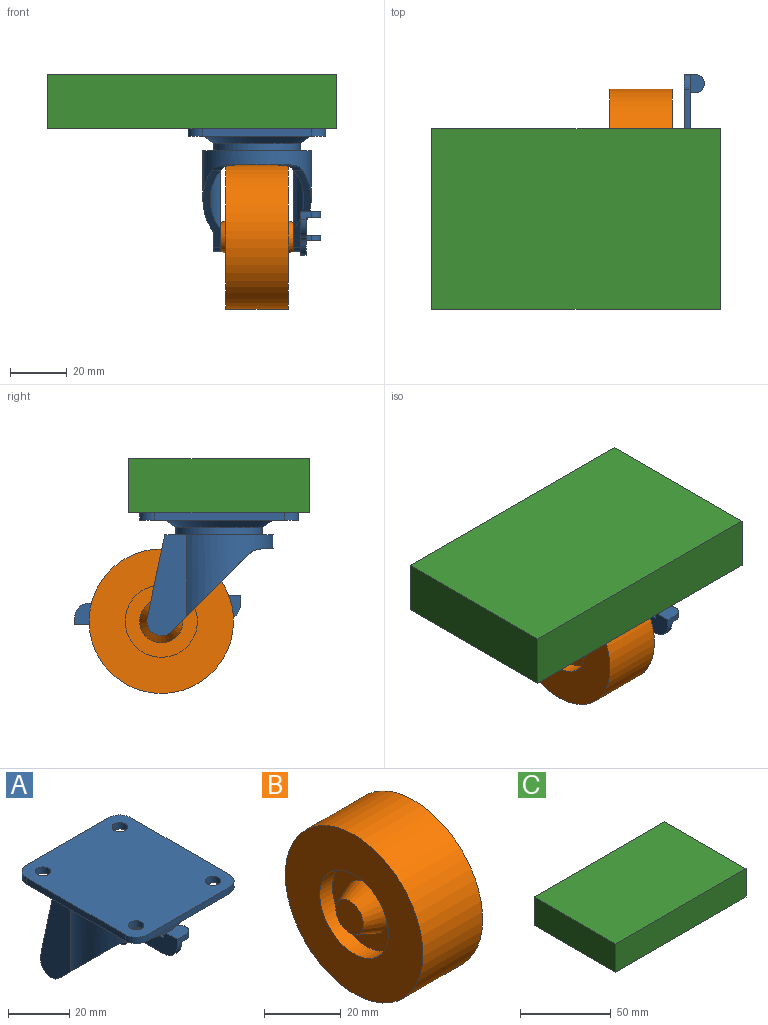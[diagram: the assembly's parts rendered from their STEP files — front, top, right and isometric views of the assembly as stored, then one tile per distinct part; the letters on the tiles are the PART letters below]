
ASSEMBLY  parts=3 mates=2
PART A: 53 faces, bbox 48.3x78.7x44.5 mm
  f0: plane 24.13x12.74mm, normal (1,0,0), area 245.6mm2, adj f5,f6,f11,f16
  f1: cylinder r=5.08mm len=8.67mm, axis (1,0,0), area 33.1mm2, adj f3,f11,f14,f17
  f2: cylinder r=6.35mm len=8.84mm, axis (1,0,0), area 18.4mm2, adj f5,f8,f9,f13
  f3: plane 27.13x27.13mm, normal (0,-0.71,-0.71), area 94.3mm2, adj f1,f5,f7,f13,f14,f17,f19,f32
  f4: plane 35.56x13.97mm, normal (-1,0,0), area 372.6mm2, adj f5,f6,f9,f10,f11
  f5: cylinder r=19.05mm len=38.1mm, axis (0,0,-1), area 1021.3mm2, adj f0,f2,f3,f4,f6,f7,f8,f9
  f6: plane 38.1x38.1mm, normal (0,0,1), area 480.4mm2, adj f0,f4,f5,f11,f37
  f7: cylinder r=6.35mm len=8.84mm, axis (1,0,0), area 18.4mm2, adj f3,f5,f8,f13
  f8: plane 23.75x4.16mm, normal (0,0,-1), area 51.9mm2, adj f2,f5,f7,f13
  f9: plane 27.13x27.13mm, normal (0,-0.71,-0.71), area 103.1mm2, adj f2,f4,f5,f10,f12,f13
  f10: cylinder r=5.08mm len=8.67mm, axis (1,0,0), area 33.1mm2, adj f4,f9,f11,f12
  f11: plane 30.48x29.43mm, normal (0,0.98,0.21), area 218.8mm2, adj f0,f1,f4,f6,f10,f12,f14,f15
  f12: plane 33.02x14.85mm, normal (1,0,0), area 375.2mm2, adj f9,f10,f11,f13,f15
  f13: cylinder r=16.51mm len=33.02mm, axis (0,0,-1), area 757.9mm2, adj f2,f3,f7,f8,f9,f12,f14,f15
  f14: plane 33.02x14.85mm, normal (-1,0,0), area 375.2mm2, adj f1,f3,f11,f13,f15
  f15: plane 36.1x33.02mm, normal (0,0,-1), area 980.7mm2, adj f11,f12,f13,f14
  f16: plane 37.68x2.03mm, normal (0,0,1), area 72.9mm2, adj f0,f5,f17,f18,f32
  f17: plane 58.42x15.24mm, normal (-1,0,0), area 308.3mm2, adj f1,f3,f11,f16,f18,f19,f20,f21
  f18: cylinder r=5.08mm len=5.08mm, axis (-1,0,0), area 16.2mm2, adj f16,f17,f31,f32
  f19: plane 8.06x2.03mm, normal (0,0,1), area 16.4mm2, adj f3,f17,f20,f32
  f20: plane 3.94x2.54mm, normal (0,1,0), area 9mm2, adj f17,f19,f21,f32,f33,f36
  f21: plane 7.11x6.35mm, normal (0,0,1), area 40.8mm2, adj f17,f20,f22,f36
  f22: plane 3.94x2.54mm, normal (0,-1,0), area 9mm2, adj f17,f21,f23,f32,f33,f36
  f23: cylinder r=6.35mm len=6.35mm, axis (-1,0,0), area 20.3mm2, adj f17,f22,f24,f32
  f24: plane 13.07x2.03mm, normal (0,0,-1), area 26.6mm2, adj f17,f23,f25,f32
  f25: cylinder r=2.54mm len=2.43mm, axis (-1,0,0), area 6.6mm2, adj f17,f24,f26,f32
  f26: cylinder r=6.35mm len=12.17mm, axis (-1,0,0), area 33.1mm2, adj f17,f25,f27,f32
  f27: cylinder r=2.54mm len=2.43mm, axis (-1,0,0), area 6.6mm2, adj f17,f26,f28,f32
  f28: plane 15.61x2.03mm, normal (0,0,-1), area 31.7mm2, adj f17,f27,f29,f32
  f29: plane 3.94x2.03mm, normal (0,-1,0), area 6.5mm2, adj f17,f28,f30,f32,f34,f35
  f30: plane 7.11x6.35mm, normal (0,0,-1), area 40.8mm2, adj f17,f29,f31,f35
  f31: plane 3.94x2.54mm, normal (0,1,0), area 9mm2, adj f17,f18,f30,f32,f34,f35
  f32: plane 58.42x13.21mm, normal (1,0,0), area 419.4mm2, adj f3,f5,f16,f18,f19,f20,f22,f23
  f33: plane 6.35x5.08mm, normal (0,0,-1), area 27.9mm2, adj f20,f22,f32,f36
  f34: plane 6.35x5.08mm, normal (0,0,1), area 27.9mm2, adj f29,f31,f32,f35
  f35: cylinder r=3.17mm len=6.35mm, axis (0,0,-1), area 20.3mm2, adj f29,f30,f31,f34
  f36: cylinder r=3.17mm len=6.35mm, axis (0,0,1), area 20.3mm2, adj f20,f21,f22,f33
  f37: cylinder r=15.24mm len=30.48mm, axis (0,0,-1), area 243.2mm2, adj f6,f38
  f38: cone r=15.24mm half-angle=56.3deg, axis (0,0,1), area 493.3mm2, adj f37,f48
  f39: plane 38.1x2.54mm, normal (0,1,0), area 96.8mm2, adj f47,f48,f49,f52
  f40: plane 45.72x2.54mm, normal (-1,0,0), area 116.1mm2, adj f47,f48,f49,f50
  f41: plane 38.1x2.54mm, normal (0,-1,0), area 96.8mm2, adj f47,f48,f50,f51
  f42: cylinder r=2.54mm len=5.08mm, axis (0,0,-1), area 40.5mm2, adj f47,f48
  f43: cylinder r=2.54mm len=5.08mm, axis (0,0,-1), area 40.5mm2, adj f47,f48
  f44: cylinder r=2.54mm len=5.08mm, axis (0,0,-1), area 40.5mm2, adj f47,f48
  f45: cylinder r=2.54mm len=5.08mm, axis (0,0,-1), area 40.5mm2, adj f47,f48
  f46: plane 45.72x2.54mm, normal (1,0,0), area 116.1mm2, adj f47,f48,f51,f52
  f47: plane 55.88x48.26mm, normal (0,0,1), area 2593.5mm2, adj f39,f40,f41,f42,f43,f44,f45,f46
  f48: plane 55.88x48.26mm, normal (0,0,-1), area 1453.5mm2, adj f38,f39,f40,f41,f42,f43,f44,f45
  f49: cylinder r=5.08mm len=5.08mm, axis (0,0,1), area 20.3mm2, adj f39,f40,f47,f48
  f50: cylinder r=5.08mm len=5.08mm, axis (0,0,-1), area 20.3mm2, adj f40,f41,f47,f48
  f51: cylinder r=5.08mm len=5.08mm, axis (0,0,1), area 20.3mm2, adj f41,f46,f47,f48
  f52: cylinder r=5.08mm len=5.08mm, axis (0,0,-1), area 20.3mm2, adj f39,f46,f47,f48
PART B: 11 faces, bbox 25.4x50.8x50.8 mm
  f0: cone r=5.08mm half-angle=21.8deg, axis (1,0,0), area 272.9mm2, adj f1,f10
  f1: plane 10.16x10.16mm, normal (-1,0,0), area 81.1mm2, adj f0
  f2: plane 10.16x10.16mm, normal (1,0,0), area 81.1mm2, adj f3
  f3: cone r=5.08mm half-angle=21.8deg, axis (-1,0,0), area 272.9mm2, adj f2,f4
  f4: plane 25.4x25.4mm, normal (1,0,0), area 324.3mm2, adj f3,f5
  f5: cylinder r=12.7mm len=25.4mm, axis (-1,0,0), area 375mm2, adj f4,f6
  f6: plane 50.8x50.8mm, normal (1,0,0), area 1520.1mm2, adj f5,f7
  f7: cylinder r=25.4mm len=50.8mm, axis (-1,0,0), area 3526.7mm2, adj f6,f8
  f8: plane 50.8x50.8mm, normal (-1,0,0), area 1520.1mm2, adj f7,f9
  f9: cylinder r=12.7mm len=25.4mm, axis (-1,0,0), area 375mm2, adj f8,f10
  f10: plane 25.4x25.4mm, normal (-1,0,0), area 324.3mm2, adj f0,f9
PART C: 6 faces, bbox 101.6x63.5x19.1 mm
  f0: plane 101.6x19.05mm, normal (0,-1,0), area 1935.5mm2, adj f1,f3,f4,f5
  f1: plane 63.5x19.05mm, normal (1,0,0), area 1209.7mm2, adj f0,f2,f4,f5
  f2: plane 101.6x19.05mm, normal (0,1,0), area 1935.5mm2, adj f1,f3,f4,f5
  f3: plane 63.5x19.05mm, normal (-1,0,0), area 1209.7mm2, adj f0,f2,f4,f5
  f4: plane 101.6x63.5mm, normal (0,0,1), area 6451.6mm2, adj f0,f1,f2,f3
  f5: plane 101.6x63.5mm, normal (0,0,-1), area 6451.6mm2, adj f0,f1,f2,f3
PLACE A at identity fixed
PLACE B at identity
PLACE C t=(27.94,-52.07,38.1)mm
MATE revolute B.f0 <-> A.f1  axis (1,0,0) through (12.7,0,0)mm
MATE fastened A.f43 <-> C.f5  axis (0,0,1) through (17.78,-41.91,38.1)mm
